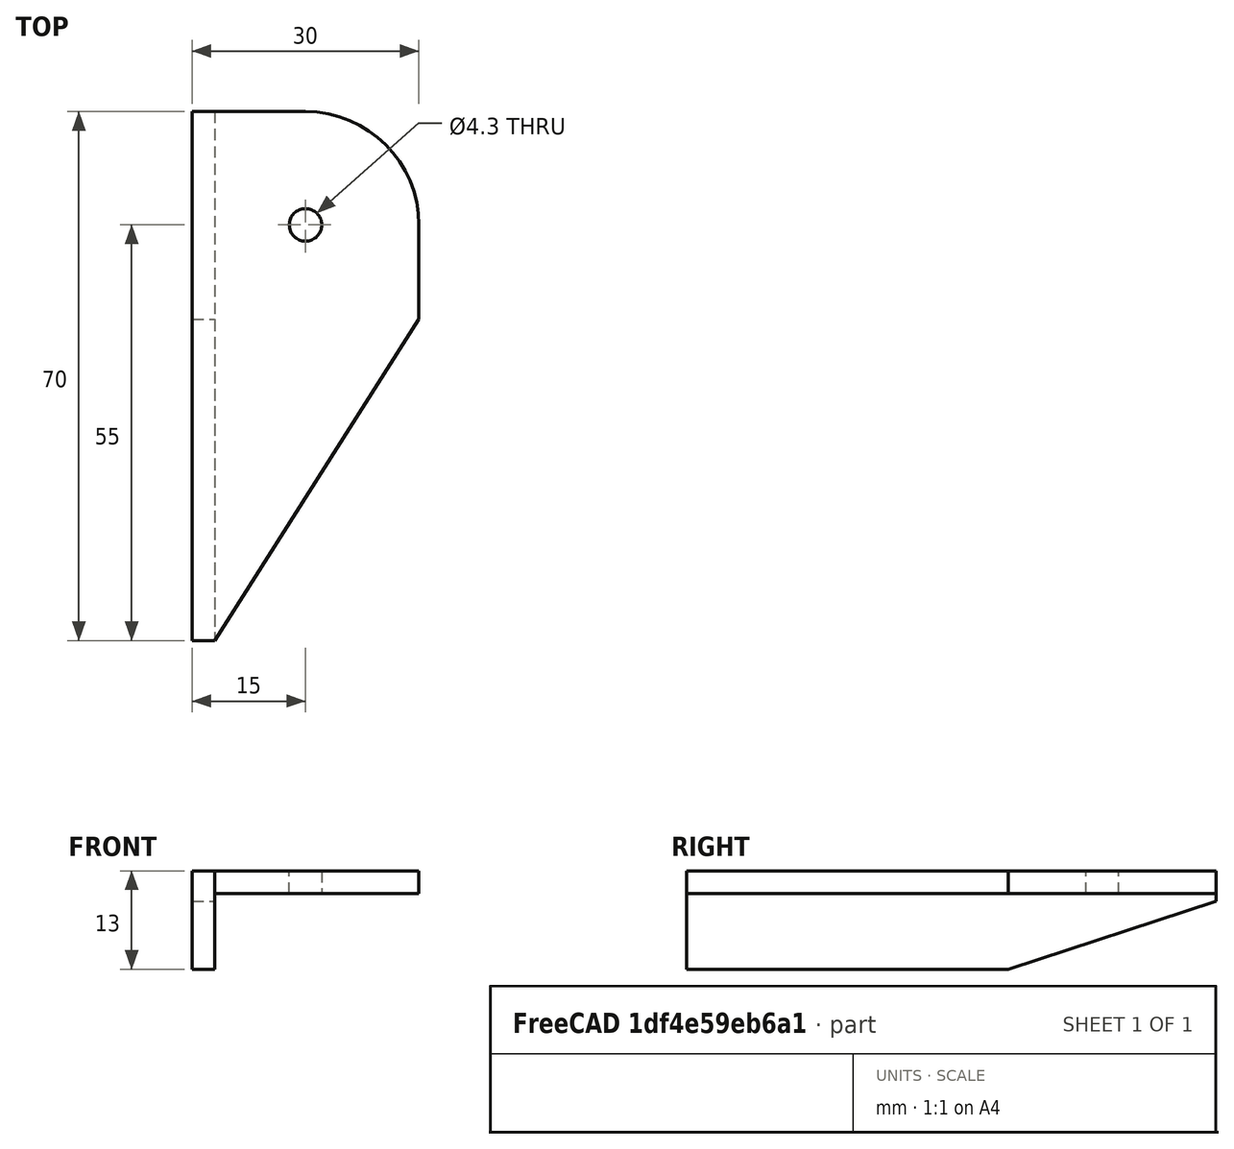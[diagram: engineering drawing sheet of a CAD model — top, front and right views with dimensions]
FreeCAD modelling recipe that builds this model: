
FCSTD DOCUMENT  (FreeCAD 1.0R39319 (Git))
Label: 18_lamella_l_holder
License: All rights reserved
LicenseURL: http://en.wikipedia.org/wiki/All_rights_reserved
objects: TechDraw::DrawViewDimension×10, TechDraw::DrawProjGroupItem×7, Sketcher::SketchObject×5, PartDesign::Pocket×4, TechDraw::DrawViewAnnotation×4, TechDraw::DrawViewBalloon×2, PartDesign::Pad×1, PartDesign::Fillet×1, TechDraw::DrawSVGTemplate×1, PartDesign::Chamfer×1, PartDesign::Body×1, TechDraw::DrawProjGroup×1, TechDraw::DrawPage×1
note: 50 computed .brp shape members not serialized (recipe doc carries the construction recipe); baked Part::Feature solids carry a one-line shape summary decoded from their .brp

FEATURE [Sketcher::SketchObject] Sketch
  ArcFitTolerance = 1e-06
  AttachmentSupport = -> [XZ_Plane]
  FullyConstrained = true
  MakeInternals = false
  MapMode = 5
  Placement = pos=(0,0,0) rot=(1,0,0;1.5708rad)
  sketch-geometry (6):
    g0: LineSegment StartX=0 StartY=0 StartZ=0 EndX=0 EndY=-13 EndZ=0
    g1: LineSegment StartX=0 StartY=-13 StartZ=0 EndX=3 EndY=-13 EndZ=0
    g2: LineSegment StartX=3 StartY=-13 StartZ=0 EndX=3 EndY=-3 EndZ=0
    g3: LineSegment StartX=3 StartY=-3 StartZ=0 EndX=30 EndY=-3 EndZ=0
    g4: LineSegment StartX=30 StartY=-3 StartZ=0 EndX=30 EndY=0 EndZ=0
    g5: LineSegment StartX=30 StartY=0 StartZ=0 EndX=0 EndY=0 EndZ=0
  constraints (17):
    c: Coincident(g-1,g0)
    c: Vertical(g0)
    c: Coincident(g0,g1)
    c: Horizontal(g1)
    c: Coincident(g1,g2)
    c: Vertical(g2)
    c: Coincident(g2,g3)
    c: Horizontal(g3)
    c: Coincident(g3,g4)
    c: PointOnObject(g4,g-1)
    c: Coincident(g4,g5)
    c: Coincident(g5,g0)
    c: Equal(g1,g4)
    c: Vertical(g4)
    c: Distance(g1,g1) = 3
    c: DistanceX(g5,g5) = 30
    c: DistanceY(g2,g2) = 10
FEATURE [PartDesign::Pad] Pad
  Direction = (0,-1,2e-16)
  Length = 70
  Length2 = 10
  Placement = pos=(0,0,0) rot=(1,0,0;1.5708rad)
  Profile = -> Sketch
  ReferenceAxis = -> Sketch [N_Axis]
  Suppressed = false
  Type = 0
FEATURE [Sketcher::SketchObject] Sketch001
  ArcFitTolerance = 1e-06
  AttachmentSupport = -> [XY_Plane]
  ExternalGeometry = -> [Pad]
  FullyConstrained = true
  MakeInternals = false
  MapMode = 5
  sketch-geometry (3):
    g0: LineSegment StartX=30 StartY=-27.5 StartZ=0 EndX=3 EndY=-70 EndZ=0
    g1: LineSegment StartX=3 StartY=-70 StartZ=0 EndX=30 EndY=-70 EndZ=0
    g2: LineSegment StartX=30 StartY=-27.5 StartZ=0 EndX=30 EndY=-70 EndZ=0
  constraints (8):
    c: PointOnObject(g0,g-3)
    c: Coincident(g0,g1)
    c: PointOnObject(g0,g-4)
    c: Coincident(g2,g0)
    c: Coincident(g2,g1)
    c: DistanceY(g2,g2) = 42.5
    c: Coincident(g1,g-4)
    c: Distance(g-3,g0) = 3
FEATURE [PartDesign::Pocket] Pocket
  BaseFeature = -> Pad
  Direction = (0,0,-1)
  Length = 5
  Length2 = 5
  Placement = pos=(0,0,0) rot=(1,0,0;1.5708rad)
  Profile = -> Sketch001
  ReferenceAxis = -> Sketch001 [N_Axis]
  Suppressed = false
  Type = 0
FEATURE [Sketcher::SketchObject] Sketch002
  ArcFitTolerance = 1e-06
  AttachmentSupport = -> [XY_Plane]
  ExternalGeometry = -> [Pocket]
  FullyConstrained = true
  MakeInternals = false
  MapMode = 5
  sketch-geometry (2):
    g0: LineSegment [constr] StartX=15 StartY=0 StartZ=0 EndX=15 EndY=-15 EndZ=0
    g1: Circle CenterX=15 CenterY=-15 CenterZ=0 NormalX=0 NormalY=0 NormalZ=1 AngleXU=0 Radius=2.15
  constraints (5):
    c: Symmetric(g-3,g-3,g0)
    c: Vertical(g0)
    c: Coincident(g1,g0)
    c: Diameter(g1) = 4.3
    c: DistanceY(g-4,g0) = 55
FEATURE [PartDesign::Pocket] Pocket001
  BaseFeature = -> Pocket
  Direction = (0,0,-1)
  Length = 5
  Length2 = 5
  Placement = pos=(0,0,0) rot=(1,0,0;1.5708rad)
  Profile = -> Sketch002
  ReferenceAxis = -> Sketch002 [N_Axis]
  Suppressed = false
  Type = 0
FEATURE [PartDesign::Fillet] Fillet
  Base = -> Pocket001 [Edge15]
  BaseFeature = -> Pocket001
  Placement = pos=(0,0,0) rot=(1,0,0;1.5708rad)
  Radius = 15
  SupportTransform = false
  Suppressed = false
  UseAllEdges = false
FEATURE [Sketcher::SketchObject] Sketch005
  ArcFitTolerance = 1e-06
  AttachmentSupport = -> [YZ_Plane]
  ExternalGeometry = -> [Fillet]
  FullyConstrained = true
  MakeInternals = false
  MapMode = 5
  Placement = pos=(0,0,0) rot=(0.57735,0.57735,0.57735;2.0944rad)
  sketch-geometry (3):
    g0: LineSegment StartX=-9e-16 StartY=-4 StartZ=0 EndX=-27.5 EndY=-13 EndZ=0
    g1: LineSegment StartX=-2.9e-15 StartY=-13 StartZ=0 EndX=-9e-16 EndY=-4 EndZ=0
    g2: LineSegment StartX=-2.9e-15 StartY=-13 StartZ=0 EndX=-27.5 EndY=-13 EndZ=0
  constraints (9):
    c: PointOnObject(g0,g-4)
    c: Coincident(g1,g0)
    c: Distance(g0,g-1) = 4
    c: Coincident(g2,g1)
    c: Coincident(g2,g0)
    c: PointOnObject(g0,g-3)
    c: DistanceX(g2,g2) = 27.5
    c: Coincident(g1,g-4)
    c: DistanceX(g-3,g0) = 42.5
FEATURE [PartDesign::Pocket] Pocket002
  BaseFeature = -> Fillet
  Direction = (-1,0,0)
  Length = 5
  Length2 = 5
  Placement = pos=(0,0,0) rot=(1,0,0;1.5708rad)
  Profile = -> Sketch005
  ReferenceAxis = -> Sketch005 [N_Axis]
  Reversed = true
  Suppressed = false
  Type = 0
FEATURE [Sketcher::SketchObject] Sketch006
  ArcFitTolerance = 1e-06
  AttachmentSupport = -> [YZ_Plane]
  ExternalGeometry = -> [Pocket002]
  FullyConstrained = true
  MakeInternals = false
  MapMode = 5
  Placement = pos=(0,0,0) rot=(0.57735,0.57735,0.57735;2.0944rad)
  sketch-geometry (4):
    g0: LineSegment [constr] StartX=-27.5 StartY=-13 StartZ=0 EndX=-27.5 EndY=-8 EndZ=0
    g1: LineSegment [constr] StartX=-27.5 StartY=-8 StartZ=0 EndX=-70 EndY=-8 EndZ=0
    g2: Circle CenterX=-59 CenterY=-8 CenterZ=0 NormalX=0 NormalY=0 NormalZ=1 AngleXU=0 Radius=2.5
    g3: Circle CenterX=-39 CenterY=-8 CenterZ=0 NormalX=0 NormalY=0 NormalZ=1 AngleXU=0 Radius=2.5
  constraints (14):
    c: Coincident(g0,g-3)
    c: Vertical(g0)
    c: Coincident(g1,g0)
    c: PointOnObject(g1,g-4)
    c: Horizontal(g1)
    c: Distance(g0,g0) = 5
    c: PointOnObject(g2,g1)
    c: Diameter(g2) = 5
    c: PointOnObject(g3,g1)
    c: Equal(g2,g3)
    c: DistanceX(g2,g3) = 20
    c: DistanceX(g3,g-1) = 39
    c: DistanceX(g1,g2) = 11
    c: Distance(g0,g3) = 11.5
FEATURE [PartDesign::Pocket] Pocket003
  BaseFeature = -> Pocket002
  Direction = (-1,0,0)
  Length = 5
  Length2 = 5
  Placement = pos=(0,0,0) rot=(1,0,0;1.5708rad)
  Profile = -> Sketch006
  ReferenceAxis = -> Sketch006 [N_Axis]
  Reversed = true
  Suppressed = true
  Type = 0
FEATURE [TechDraw::DrawSVGTemplate] Template
  EditableTexts = AuthorName=Matthias Mosimann; CheckDate=N/A; CreationDate=11/04/2026; DrawingNumber=1.0; FC-Title=Lamellenhalter; SheetNumber=1 / 1; Subtitle=(Ohne Nieten); SupervisorName=N/A; Weight=N/A; scale=1 : 1
  Height = 297
  Orientation = 1
  Template = C:/Program Files/FreeCAD 1.0/data/Mod/TechDraw/Templates/A3_Landscape_TD.svg
  Width = 420
FEATURE [PartDesign::Chamfer] Chamfer
  Angle = 45
  Base = -> Pocket002 [Edge7]
  BaseFeature = -> Pocket002
  ChamferType = 0
  FlipDirection = false
  Placement = pos=(0,0,0) rot=(1,0,0;1.5708rad)
  Size = 2
  Size2 = 1
  SupportTransform = false
  Suppressed = true
  UseAllEdges = false
FEATURE [PartDesign::Body] Body
  AllowCompound = false
  Group = -> [Sketch,Pad,Sketch001,Pocket,Sketch002,Pocket001,Fillet,Sketch005,Pocket002,Sketch006,Pocket003,Chamfer]
  Origin = -> Origin
  Tip = -> Chamfer
FEATURE [TechDraw::DrawProjGroupItem] View  label="Front"
  CoarseView = false
  Direction = (0,-1,0)
  Focus = 100
  HardHidden = false
  IsoCount = 0
  IsoHidden = false
  IsoVisible = false
  LockPosition = true
  Perspective = false
  Rotation = 0
  RotationVector = (1,0,0)
  ScaleType = 2
  ScrubCount = 1
  SeamHidden = false
  SeamVisible = true
  SmoothHidden = false
  SmoothVisible = true
  Source = -> [Body]
  Type = 0
  X = 0
  XDirection = (1,0,0)
  Y = 0
FEATURE [TechDraw::DrawProjGroupItem] ProjItem  label="Right"
  CoarseView = false
  Direction = (1,-1e-16,0)
  Focus = 100
  HardHidden = false
  IsoCount = 0
  IsoHidden = false
  IsoVisible = false
  LockPosition = true
  Perspective = false
  Rotation = 0
  RotationVector = (1,0,0)
  ScaleType = 0
  ScrubCount = 1
  SeamHidden = false
  SeamVisible = true
  SmoothHidden = false
  SmoothVisible = true
  Source = -> [Body]
  Type = 2
  X = -78.1882
  XDirection = (1e-16,1,0)
  Y = 0
FEATURE [TechDraw::DrawProjGroupItem] ProjItem001  label="Left"
  CoarseView = false
  Direction = (-1,-1e-16,0)
  Focus = 100
  HardHidden = false
  IsoCount = 0
  IsoHidden = false
  IsoVisible = false
  LockPosition = true
  Perspective = false
  Rotation = 0
  RotationVector = (1,0,0)
  ScaleType = 0
  ScrubCount = 1
  SeamHidden = false
  SeamVisible = true
  SmoothHidden = false
  SmoothVisible = true
  Source = -> [Body]
  Type = 1
  X = 92.6952
  XDirection = (1e-16,-1,0)
  Y = 0
FEATURE [TechDraw::DrawProjGroupItem] ProjItem002  label="Bottom"
  CoarseView = false
  Direction = (0,0,-1)
  Focus = 100
  HardHidden = false
  IsoCount = 0
  IsoHidden = false
  IsoVisible = false
  LockPosition = true
  Perspective = false
  Rotation = 0
  RotationVector = (1,0,0)
  ScaleType = 0
  ScrubCount = 1
  SeamHidden = false
  SeamVisible = true
  SmoothHidden = false
  SmoothVisible = true
  Source = -> [Body]
  Type = 5
  X = 0
  XDirection = (1,0,0)
  Y = 63.8854
FEATURE [TechDraw::DrawProjGroupItem] ProjItem003  label="Top"
  CoarseView = false
  Direction = (0,0,1)
  Focus = 100
  HardHidden = true
  IsoCount = 0
  IsoHidden = false
  IsoVisible = false
  LockPosition = true
  Perspective = false
  Rotation = 0
  RotationVector = (1,0,0)
  ScaleType = 0
  ScrubCount = 1
  SeamHidden = false
  SeamVisible = true
  SmoothHidden = false
  SmoothVisible = true
  Source = -> [Body]
  Type = 4
  X = 0
  XDirection = (1,0,0)
  Y = -71.4466
FEATURE [TechDraw::DrawProjGroupItem] ProjItem004  label="FrontTopLeft"
  CoarseView = false
  Direction = (-0.57735,-0.57735,0.57735)
  Focus = 100
  HardHidden = false
  IsoCount = 0
  IsoHidden = false
  IsoVisible = false
  LockPosition = true
  Perspective = false
  Rotation = 0
  RotationVector = (1,0,0)
  ScaleType = 0
  ScrubCount = 1
  SeamHidden = false
  SeamVisible = true
  SmoothHidden = false
  SmoothVisible = true
  Source = -> [Body]
  Type = 6
  X = 92.6952
  XDirection = (0.707107,-0.707107,0)
  Y = -58.2584
FEATURE [TechDraw::DrawProjGroupItem] ProjItem005  label="FrontBottomLeft"
  CoarseView = false
  Direction = (-0.57735,-0.57735,-0.57735)
  Focus = 100
  HardHidden = false
  IsoCount = 0
  IsoHidden = false
  IsoVisible = false
  LockPosition = true
  Perspective = false
  Rotation = 0
  RotationVector = (1,0,0)
  ScaleType = 0
  ScrubCount = 1
  SeamHidden = false
  SeamVisible = true
  SmoothHidden = false
  SmoothVisible = true
  Source = -> [Body]
  Type = 8
  X = 92.6952
  XDirection = (0.707107,-0.707107,0)
  Y = 54.7416
FEATURE [TechDraw::DrawProjGroup] ProjGroup
  Anchor = -> View
  AutoDistribute = true
  LockPosition = false
  ProjectionType = 0
  Rotation = 0
  ScaleType = 0
  Source = -> [Body]
  Views = -> [View,ProjItem,ProjItem001,ProjItem002,ProjItem003,ProjItem004,ProjItem005]
  X = 135.616
  Y = 180.587
  spacingX = 15
  spacingY = 15
FEATURE [TechDraw::DrawViewDimension] Dimension
  AngleOverride = false
  Arbitrary = false
  ArbitraryTolerances = false
  BoxCorners = (2) [(-35,-6.5,-1e-07),(35,6.5,1e-07)]
  EqualTolerance = true
  ExtensionAngle = 0
  FormatSpec = %.2w
  FormatSpecOverTolerance = %+.2w
  FormatSpecUnderTolerance = %+.2w
  Inverted = false
  LineAngle = 0
  LockPosition = false
  MeasureType = 1
  OverTolerance = 0
  References2D = -> [ProjItem]
  Rotation = 0
  ScaleType = 0
  TheoreticalExact = false
  Type = 0
  UnderTolerance = 0
  X = -3.06583
  Y = 29.7015
FEATURE [TechDraw::DrawViewDimension] Dimension001
  AngleOverride = false
  Arbitrary = false
  ArbitraryTolerances = false
  BoxCorners = (2) [(-35,-6.5,-1e-07),(35,6.5,1e-07)]
  EqualTolerance = true
  ExtensionAngle = 0
  FormatSpec = %.2w
  FormatSpecOverTolerance = %+.2w
  FormatSpecUnderTolerance = %+.2w
  Inverted = false
  LineAngle = 0
  LockPosition = false
  MeasureType = 1
  OverTolerance = 0
  References2D = -> [ProjItem]
  Rotation = 0
  ScaleType = 0
  TheoreticalExact = false
  Type = 0
  UnderTolerance = 0
  X = -46.0905
  Y = 18.5277
FEATURE [TechDraw::DrawViewDimension] Dimension002
  AngleOverride = false
  Arbitrary = false
  ArbitraryTolerances = false
  BoxCorners = (2) [(-35,-6.5,-1e-07),(35,6.5,1e-07)]
  EqualTolerance = true
  ExtensionAngle = 0
  FormatSpec = %.2w
  FormatSpecOverTolerance = %+.2w
  FormatSpecUnderTolerance = %+.2w
  Inverted = false
  LineAngle = 0
  LockPosition = false
  MeasureType = 1
  OverTolerance = 0
  References2D = -> [ProjItem]
  Rotation = 0
  ScaleType = 0
  TheoreticalExact = false
  Type = 0
  UnderTolerance = 0
  X = 38.0113
  Y = -16.5806
FEATURE [TechDraw::DrawViewDimension] Dimension003
  AngleOverride = false
  Arbitrary = false
  ArbitraryTolerances = false
  BoxCorners = (2) [(-35,-6.5,-1e-07),(35,6.5,1e-07)]
  EqualTolerance = true
  ExtensionAngle = 0
  FormatSpec = %.2w
  FormatSpecOverTolerance = %+.2w
  FormatSpecUnderTolerance = %+.2w
  Inverted = false
  LineAngle = 0
  LockPosition = false
  MeasureType = 1
  OverTolerance = 0
  References2D = -> [ProjItem]
  Rotation = 0
  ScaleType = 0
  TheoreticalExact = false
  Type = 1
  UnderTolerance = 0
  X = 24.3962
  Y = -14.0118
FEATURE [TechDraw::DrawViewDimension] Dimension004
  AngleOverride = false
  Arbitrary = false
  ArbitraryTolerances = false
  BoxCorners = (2) [(-15,-6.5,0),(15,6.5,0)]
  EqualTolerance = true
  ExtensionAngle = 0
  FormatSpec = %.2w
  FormatSpecOverTolerance = %+.2w
  FormatSpecUnderTolerance = %+.2w
  Inverted = false
  LineAngle = 0
  LockPosition = false
  MeasureType = 1
  OverTolerance = 0
  References2D = -> [View]
  Rotation = 0
  ScaleType = 0
  TheoreticalExact = false
  Type = 1
  UnderTolerance = 0
  X = 30.5643
  Y = -14.0354
FEATURE [TechDraw::DrawViewDimension] Dimension005
  AngleOverride = false
  Arbitrary = false
  ArbitraryTolerances = false
  BoxCorners = (2) [(-15,-6.5,0),(15,6.5,0)]
  EqualTolerance = true
  ExtensionAngle = 0
  FormatSpec = %.2w
  FormatSpecOverTolerance = %+.2w
  FormatSpecUnderTolerance = %+.2w
  Inverted = false
  LineAngle = 0
  LockPosition = false
  MeasureType = 1
  OverTolerance = 0
  References2D = -> [View]
  Rotation = 0
  ScaleType = 0
  TheoreticalExact = false
  Type = 0
  UnderTolerance = 0
  X = 24.4094
  Y = 10.317
FEATURE [TechDraw::DrawViewDimension] Dimension006
  AngleOverride = false
  Arbitrary = false
  ArbitraryTolerances = false
  BoxCorners = (2) [(-15,-35,0),(15,35,0)]
  EqualTolerance = true
  ExtensionAngle = 0
  FormatSpec = %.2w
  FormatSpecOverTolerance = %+.2w
  FormatSpecUnderTolerance = %+.2w
  Inverted = false
  LineAngle = 0
  LockPosition = false
  MeasureType = 1
  OverTolerance = 0
  References2D = -> [ProjItem002]
  Rotation = 0
  ScaleType = 0
  TheoreticalExact = false
  Type = 0
  UnderTolerance = 0
  X = 16.0576
  Y = -27.5
FEATURE [TechDraw::DrawViewDimension] Dimension007
  AngleOverride = false
  Arbitrary = false
  ArbitraryTolerances = false
  BoxCorners = (2) [(-15,-35,0),(15,35,0)]
  EqualTolerance = true
  ExtensionAngle = 0
  FormatSpec = %.2w
  FormatSpecOverTolerance = %+.2w
  FormatSpecUnderTolerance = %+.2w
  Inverted = false
  LineAngle = 0
  LockPosition = false
  MeasureType = 1
  OverTolerance = 0
  References2D = -> [ProjItem002]
  Rotation = 0
  ScaleType = 0
  TheoreticalExact = false
  Type = 0
  UnderTolerance = 0
  X = -24.5026
  Y = -30.8764
FEATURE [TechDraw::DrawViewDimension] Dimension008
  AngleOverride = false
  Arbitrary = false
  ArbitraryTolerances = false
  BoxCorners = (2) [(-15,-35,0),(15,35,0)]
  EqualTolerance = true
  ExtensionAngle = 0
  FormatSpec = ⌀%.2w
  FormatSpecOverTolerance = %+.2w
  FormatSpecUnderTolerance = %+.2w
  Inverted = false
  LineAngle = 0
  LockPosition = false
  MeasureType = 1
  OverTolerance = 0
  References2D = -> [ProjItem002]
  Rotation = 0
  ScaleType = 0
  TheoreticalExact = false
  Type = 5
  UnderTolerance = 0
  X = 31.4117
  Y = 3.05728
FEATURE [TechDraw::DrawViewBalloon] Balloon
  BubbleShape = 0
  EndType = 0
  EndTypeScale = 1
  KinkLength = 5
  LockPosition = false
  OriginX = -2.15
  OriginY = -20
  Rotation = 0
  ScaleType = 0
  ShapeScale = 1
  SourceView = -> ProjItem002
  Text = 1
  TextWrapLen = -1
  X = -28.8549
  Y = -1.73223
FEATURE [TechDraw::DrawViewDimension] Dimension009
  AngleOverride = false
  Arbitrary = false
  ArbitraryTolerances = false
  BoxCorners = (2) [(-15,-35,0),(15,35,0)]
  EqualTolerance = true
  ExtensionAngle = 0
  FormatSpec = %.2w
  FormatSpecOverTolerance = %+.2w
  FormatSpecUnderTolerance = %+.2w
  Inverted = false
  LineAngle = 0
  LockPosition = false
  MeasureType = 1
  OverTolerance = 0
  References2D = -> [ProjItem002]
  Rotation = 0
  ScaleType = 0
  TheoreticalExact = false
  Type = 0
  UnderTolerance = 0
  X = 16.0576
  Y = 22.6923
FEATURE [TechDraw::DrawViewBalloon] Balloon001
  BubbleShape = 0
  EndType = 0
  EndTypeScale = 1
  KinkLength = 5
  LockPosition = false
  OriginX = 116.055
  OriginY = -6.24717
  Rotation = 0
  ScaleType = 0
  ShapeScale = 1
  SourceView = -> ProjGroup
  Text = 2
  TextWrapLen = -1
  X = 138.817
  Y = -26.9841
FEATURE [TechDraw::DrawViewAnnotation] Annotation
  Font = osifont
  LineSpace = 80
  LockPosition = false
  MaxWidth = 120
  Rotation = 0
  ScaleType = 0
  Text = (1) Durchgangsloch M4 fein (kann auch grösser sein M5/M6). Achtung, muss aber dann ingesamt angepasst werden. | (2) Teil wird punktgeschweist angebracht, an Lamelle (siehe andere Zeichnung)
  TextSize = 3
  TextStyle = 0
  X = 340.748
  Y = 217.555
FEATURE [TechDraw::DrawViewAnnotation] Annotation001
  Font = osifont
  LineSpace = 80
  LockPosition = false
  MaxWidth = 120
  Rotation = 0
  ScaleType = 0
  Text = (1) Durchgangsloch M4 fein (kann auch grösser sein M5/M6). Achtung, muss aber dann ingesamt angepasst werden. | (2) Teil wird punktgeschweist angebracht, an Lamelle (siehe andere Zeichnung) | (3) Senkung ist auf M4 angepasst.
  TextSize = 3
  TextStyle = 0
  X = 341.213
  Y = 227.096
FEATURE [TechDraw::DrawViewAnnotation] Annotation002
  Font = osifont
  LineSpace = 80
  LockPosition = false
  MaxWidth = 120
  Rotation = 0
  ScaleType = 0
  Text = (1) Durchgangsloch M4 fein (kann auch grösser sein M5/M6). Achtung, muss aber dann ingesamt angepasst werden. | (2) Teil wird punktgeschweist angebracht, an Lamelle (siehe andere Zeichnung) | (3) Senkung ist auf M4 angepasst.
  TextSize = 3
  TextStyle = 0
  X = 340.282
  Y = 217.555
FEATURE [TechDraw::DrawViewAnnotation] Annotation003
  Font = osifont
  LineSpace = 80
  LockPosition = false
  MaxWidth = 120
  Rotation = 0
  ScaleType = 0
  Text = Teil wird aus Standard Winkelstahl hergestellt 30mm x 30mm x 3mm. Alle Angaben in mm. 3D Ansichten können von der angegebenen Skalierungsgrösse abweichen.
  TextSize = 3
  TextStyle = 1
  X = 340.748
  Y = 258.968
FEATURE [TechDraw::DrawPage] Page
  KeepUpdated = true
  NextBalloonIndex = 9
  ProjectionType = 0
  Template = -> Template
  Views = -> [ProjGroup,Dimension,Dimension001,Dimension002,Dimension003,Dimension004,Dimension005,Dimension006,Dimension007,Dimension008,Balloon,Dimension009,Balloon001,Annotation,Annotation003]
